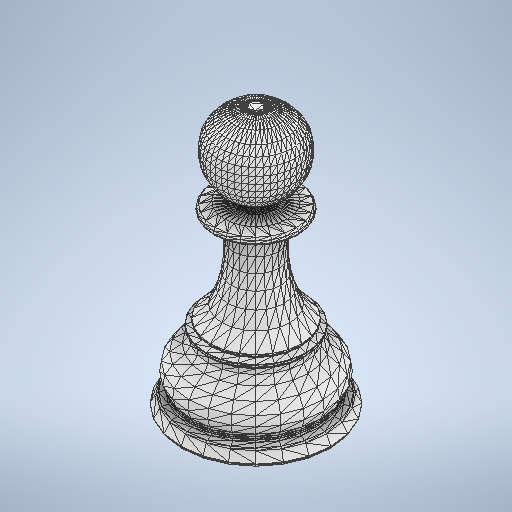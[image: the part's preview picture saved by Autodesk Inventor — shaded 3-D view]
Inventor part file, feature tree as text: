
AUTODESK INVENTOR PART (.ipt)
format: ipt  version: 2025.2 (Build 292293000, 293)  size: 7,028,736 bytes
history: native  units: mm
features: other x4, move_body x4, direct_edit x1, extrude x1, chamfer x1, sketch x1
ambient origin geometry x8: Origin, YZ Plane, XZ Plane, XY Plane, X Axis, Y Axis, Z Axis, Center Point
bodies: Solid1 (feature_tree)
feature tree (12):
  other  "ChessSet v2.ipt"
  other  "Work Axis1"
  move_body  "Move Body1"
  direct_edit  "Direct Edit1"
  move_body  "Move Body3"
  extrude  "Extrusion1"  TaperAngle=90.0deg  [1 undecoded]
  chamfer  "Chamfer1"  [1 undecoded]
  other  "Solid1::ChessSet v2.ipt"
  other  "TaggingFeature1"
  sketch  "Sketch1"  dims[d0=10.0mm d1=90.0deg d5=0.0mm d6=0.0mm d7=-5.444424mm d8=-86.441139mm d9=0.0mm d10=0.0mm d11=-7.2965mm d12=0.0mm d13=0.0mm d14=10.2mm d15=2.2mm d16=0.0mm d17=0.5mm d18=2.0mm d19=45.0deg]
  move_body  "Move1"
  move_body  "Move2"
note: 2 required parameter values undecoded (feature->parameter linkage not recoverable at this tier; creation-order binding heuristic only, values carry confidence <= 0.55)
